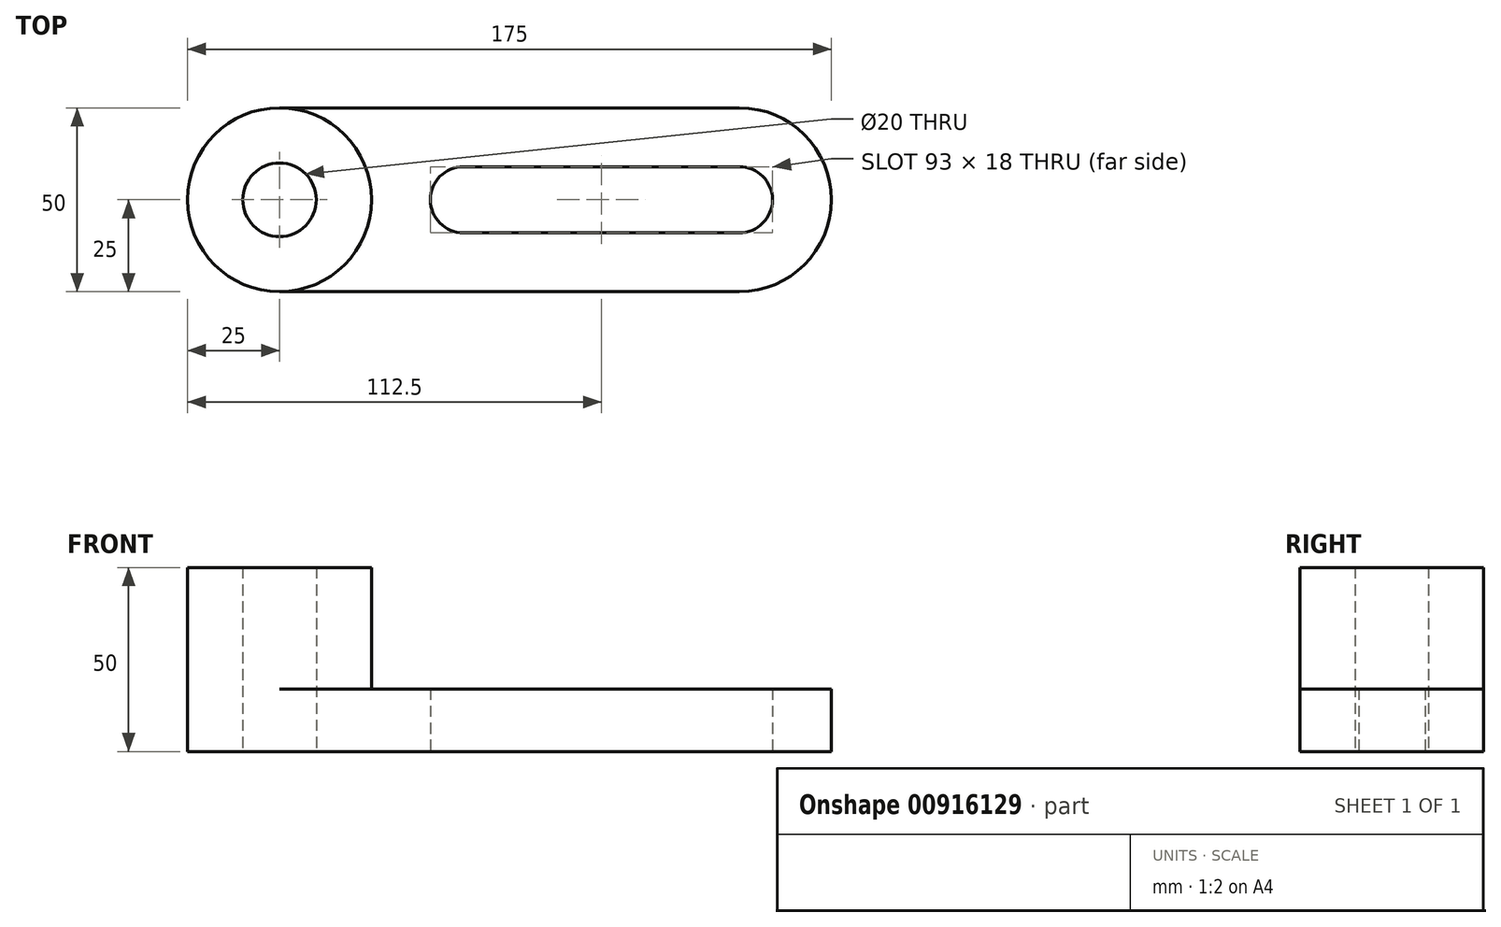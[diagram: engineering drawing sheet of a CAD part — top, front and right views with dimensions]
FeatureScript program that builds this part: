
annotation { "Feature Type Name" : "Feature", "Feature Type Description" : "" }
export const myFeature = defineFeature(function(context is Context, id is Id, definition is map)
    precondition{}
    {
        {
            var Q0;
            Q0=qCreatedBy(makeId("Top.planeOp"),FACE);
            var sketch = newSketch(context, id + "F0", { "sketchPlane" : qUnion([Q0])});
            skArc(sketch, "E0", {"start": v(0, -9) * mm, "mid": v(9, 0) * mm, "end": v(0, 9) * mm});
            skArc(sketch, "E1", {"start": v(0, -25) * mm, "mid": v(25, 0) * mm, "end": v(0, 25) * mm});
            skLineSegment(sketch, "E2", {"start": v(0, 25) * mm, "end": v(-125, 25) * mm});
            skLineSegment(sketch, "E3", {"start": v(-125, -25) * mm, "end": v(0, -25) * mm});
            skArc(sketch, "E4", {"start": v(-75, 9) * mm, "mid": v(-84, 0) * mm, "end": v(-75, -9) * mm});
            skLineSegment(sketch, "E5", {"start": v(-75, 9) * mm, "end": v(0, 9) * mm});
            skLineSegment(sketch, "E6", {"start": v(0, -9) * mm, "end": v(-75, -9) * mm});
            skCircle(sketch, "E7", {"center": v(-125, 0) * mm, "radius": 25 * mm});
            skCircle(sketch, "E8", {"center": v(-125, 0) * mm, "radius": 10 * mm});
            skSolve(sketch);
        }
        {
            var Q0;
            Q0=makeQuery(id+"F0.imprint","IMPRINT",FACE,{"disambiguationData":[TD([[makeQuery(id+"F0.imprint","IMPRINT",EDGE,{"derivedFrom":sQuery(id+"F0.wireOp",EDGE,"E0")}),-1.0]])]});
            var Q1;
            Q1=makeQuery(id+"F0.imprint","IMPRINT",FACE,{"disambiguationData":[TD([[makeQuery(id+"F0.imprint","IMPRINT",EDGE,{"derivedFrom":sQuery(id+"F0.wireOp",EDGE,"E8")}),-1.0]])]});
            extrude(context, id + "F1", {"entities" : qUnion([Q0, Q1]), "depth" : 17 * mm, "offsetDistance" : 25 * mm});
        }
        {
            var Q0;
            Q0=makeQuery(id+"F1.opExtrude","CAP_FACE",FACE,{"disambiguationData":[OSD([sQuery(id+"F0.wireOp",EDGE,"E0"),sQuery(id+"F0.wireOp",EDGE,"E1"),sQuery(id+"F0.wireOp",EDGE,"E2"),sQuery(id+"F0.wireOp",EDGE,"E3"),sQuery(id+"F0.wireOp",EDGE,"E4"),sQuery(id+"F0.wireOp",EDGE,"E5"),sQuery(id+"F0.wireOp",EDGE,"E6"),sQuery(id+"F0.wireOp",EDGE,"E7"),sQuery(id+"F0.wireOp",EDGE,"E8")])],"isStart":false});
            var sketch = newSketch(context, id + "F2", { "sketchPlane" : qUnion([Q0])});
            skCircle(sketch, "E9", {"center": v(-125, 0) * mm, "radius": 25 * mm});
            skSolve(sketch);
        }
        {
            var Q0;
            Q0=makeQuery(id+"F2.imprint","IMPRINT",FACE,{"disambiguationData":[TD([[makeQuery(id+"F2.imprint","IMPRINT",EDGE,{"derivedFrom":makeQuery(id+"F1.opExtrude","CAP_EDGE",EDGE,{"disambiguationData":[OSD([sQuery(id+"F0.wireOp",EDGE,"E8")])],"isStart":false})}),-1.0]])]});
            extrude(context, id + "F3", {"entities" : qUnion([Q0]), "operationType" : NewBodyOperationType.ADD, "depth" : 33 * mm, "offsetDistance" : 25 * mm});
        }
    });
